# Revit family: Screen-Teknion-CQCMS_Media_Rover-R2020
name_source: partatom
category: Furniture
units: mm (PartAtom-declared; Revit-internal decimal feet)

## family parameters
Always vertical = Yes
Cut with Voids When Loaded = No
OmniClass Number = 23.40.20.00
OmniClass Title = General Furniture and Specialties
Room Calculation Point = No
Shared = Yes
Work Plane-Based = No

## types (1)
- Media Rover
    Assembly Code = E2020200
    Default Elevation = 0 "
    Description = Media Rover, 66"H, Smooth Felt Back & Tray Finish
    Manufacturer = Teknion
    Manufacturer Fax = 416.661.4586
    Model = CQCMS
    Part Number = CQCMS
    Product Documentation Link = https://assets.teknion.com
    Product Line = Media Rover
    Product Page URL = https://www.teknion.com
    Series = Routes
    Sustainability Data = https://www.teknion.com
    URL = www.teknion.com
    Unit Weight URL = http://www.teknion.com
    Warranty = http://www.teknion.com

## geometry (parser evidence)
native form markers: Sweep x4
no freeform markers — native parametric forms only
